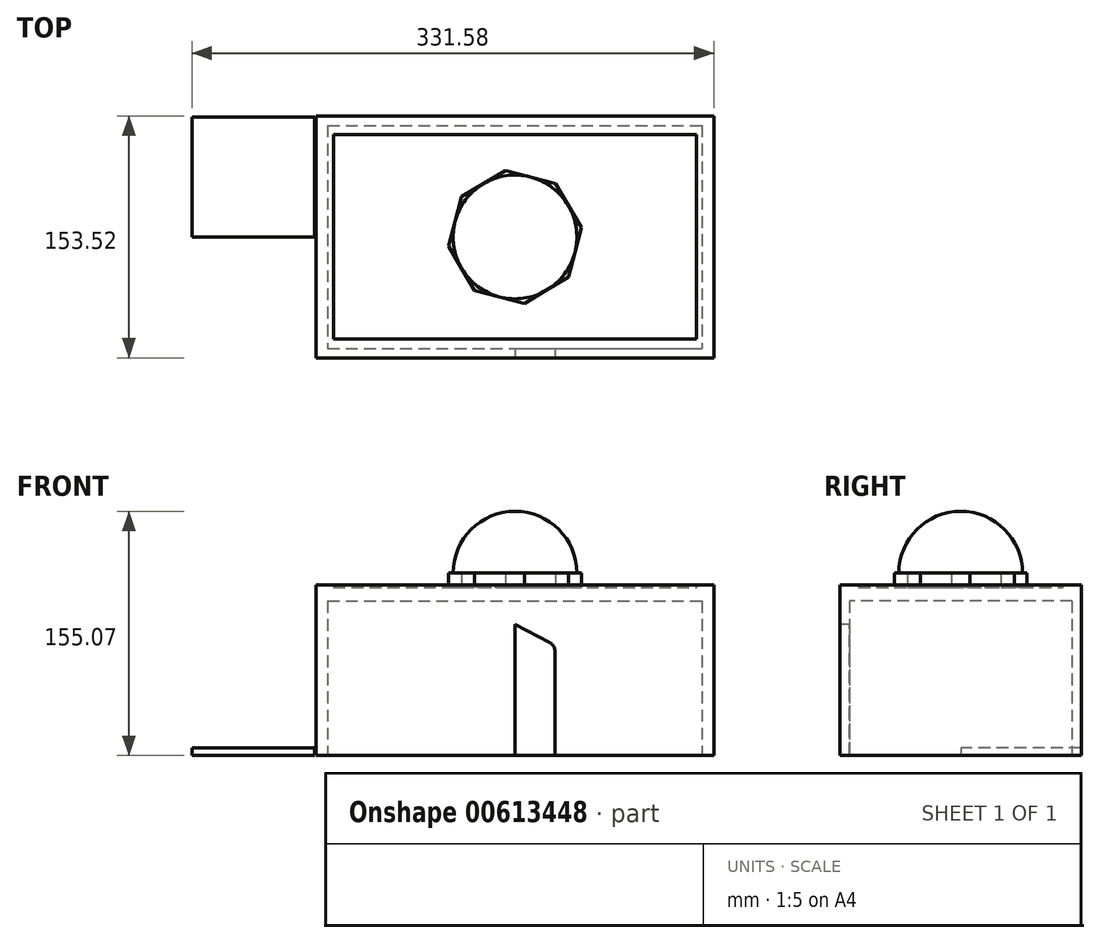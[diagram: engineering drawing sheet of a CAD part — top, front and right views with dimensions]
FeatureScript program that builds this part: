
annotation { "Feature Type Name" : "Feature", "Feature Type Description" : "" }
export const myFeature = defineFeature(function(context is Context, id is Id, definition is map)
    precondition{}
    {
        {
            var Q0;
            Q0=qCreatedBy(makeId("Top.planeOp"),FACE);
            var sketch = newSketch(context, id + "F0", { "sketchPlane" : qUnion([Q0])});
            skLineSegment(sketch, "E0.bottom", {"start": v(126.34, -76.76) * mm, "end": v(-126.34, -76.76) * mm});
            skLineSegment(sketch, "E0.top", {"start": v(126.34, 76.76) * mm, "end": v(-126.34, 76.76) * mm});
            skLineSegment(sketch, "E0.left", {"start": v(126.34, -76.76) * mm, "end": v(126.34, 76.76) * mm});
            skLineSegment(sketch, "E0.right", {"start": v(-126.34, -76.76) * mm, "end": v(-126.34, 76.76) * mm});
            skPoint(sketch, "E0.middle", {"position": v(0, 0) * mm});
            skSolve(sketch);
        }
        {
            var Q0;
            Q0 = qSketchRegion(id + "F0", true);
            extrude(context, id + "F1", {"entities" : qUnion([Q0]), "depth" : 106.63 * mm, "offsetDistance" : 25.4 * mm});
        }
        {
            var Q0;
            Q0=makeQuery(id+"F1.opExtrude","CAP_FACE",FACE,{"disambiguationData":[OSD([sQuery(id+"F0.wireOp",EDGE,"E0.bottom"),sQuery(id+"F0.wireOp",EDGE,"E0.top"),sQuery(id+"F0.wireOp",EDGE,"E0.left"),sQuery(id+"F0.wireOp",EDGE,"E0.right")])],"isStart":false});
            var sketch = newSketch(context, id + "F2", { "sketchPlane" : qUnion([Q0])});
            skCircle(sketch, "E1.cCircle", {"center": v(0, 0) * mm, "radius": 39.31 * mm, "construction": true});
            skLineSegment(sketch, "E1.0", {"start": v(-25.62, -33.98) * mm, "end": v(-42.14, -5.91) * mm});
            skLineSegment(sketch, "E1.1", {"start": v(-42.14, -5.91) * mm, "end": v(-33.98, 25.62) * mm});
            skLineSegment(sketch, "E1.2", {"start": v(-33.98, 25.62) * mm, "end": v(-5.91, 42.14) * mm});
            skLineSegment(sketch, "E1.3", {"start": v(-5.91, 42.14) * mm, "end": v(25.62, 33.98) * mm});
            skLineSegment(sketch, "E1.4", {"start": v(25.62, 33.98) * mm, "end": v(42.14, 5.91) * mm});
            skLineSegment(sketch, "E1.5", {"start": v(42.14, 5.91) * mm, "end": v(33.98, -25.62) * mm});
            skLineSegment(sketch, "E1.6", {"start": v(33.98, -25.62) * mm, "end": v(5.91, -42.14) * mm});
            skLineSegment(sketch, "E1.7", {"start": v(5.91, -42.14) * mm, "end": v(-25.62, -33.98) * mm});
            skPoint(sketch, "E1.0.midPoint", {"position": v(-33.88, -19.94) * mm});
            skSolve(sketch);
        }
        {
            var Q0;
            Q0 = qSketchRegion(id + "F2", true);
            extrude(context, id + "F3", {"entities" : qUnion([Q0]), "operationType" : NewBodyOperationType.ADD, "depth" : 9.12 * mm, "offsetDistance" : 25.4 * mm});
        }
        {
            var Q0;
            Q0=makeQuery(id+"F3.opExtrude","CAP_FACE",FACE,{"disambiguationData":[OSD([sQuery(id+"F2.wireOp",EDGE,"E1.0"),sQuery(id+"F2.wireOp",EDGE,"E1.1"),sQuery(id+"F2.wireOp",EDGE,"E1.2"),sQuery(id+"F2.wireOp",EDGE,"E1.3"),sQuery(id+"F2.wireOp",EDGE,"E1.4"),sQuery(id+"F2.wireOp",EDGE,"E1.5"),sQuery(id+"F2.wireOp",EDGE,"E1.6"),sQuery(id+"F2.wireOp",EDGE,"E1.7")])],"isStart":false});
            var sketch = newSketch(context, id + "F4", { "sketchPlane" : qUnion([Q0])});
            skCircle(sketch, "E2", {"center": v(0, 0) * mm, "radius": 39.31 * mm});
            skLineSegment(sketch, "E3", {"start": v(-42.14, -5.91) * mm, "end": v(42.14, 5.91) * mm});
            skSolve(sketch);
        }
        {
            var Q0;
            {var subQ0=sQuery(id+"F4.wireOp",EDGE,"E2");var subQ5=sQuery(id+"F4.wireOp",EDGE,"E3");var subQ6=makeQuery(id+"F4.imprint","INTERSECT",VERTEX,{"disambiguationData":[OD(0.0)],"derivedFrom":[subQ0,subQ5]});Q0=makeQuery(id+"F4.imprint","IMPRINT",FACE,{"disambiguationData":[TD([[makeQuery(id+"F4.imprint","IMPRINT",EDGE,{"disambiguationData":[TD([[subQ6,-1.0]])],"derivedFrom":subQ0}),1.0]])]});}
            var Q1;
            Q1=sQuery(id+"F4.wireOp",EDGE,"E3");
            revolve(context, id + "F5", {"operationType" : NewBodyOperationType.ADD, "entities" : qUnion([Q0]), "axis" : qUnion([Q1]), "revolveType" : RevolveType.FULL});
        }
        {
            var Q0;
            Q0=makeQuery(id+"F1.opExtrude","CAP_FACE",FACE,{"disambiguationData":[OSD([sQuery(id+"F0.wireOp",EDGE,"E0.bottom"),sQuery(id+"F0.wireOp",EDGE,"E0.top"),sQuery(id+"F0.wireOp",EDGE,"E0.left"),sQuery(id+"F0.wireOp",EDGE,"E0.right")])],"isStart":false});
            var sketch = newSketch(context, id + "F6", { "sketchPlane" : qUnion([Q0])});
            skLineSegment(sketch, "E4.bottom", {"start": v(-115.35, -64.9) * mm, "end": v(115.35, -64.9) * mm});
            skLineSegment(sketch, "E4.top", {"start": v(-115.35, 64.9) * mm, "end": v(115.35, 64.9) * mm});
            skLineSegment(sketch, "E4.left", {"start": v(-115.35, -64.9) * mm, "end": v(-115.35, 64.9) * mm});
            skLineSegment(sketch, "E4.right", {"start": v(115.35, -64.9) * mm, "end": v(115.35, 64.9) * mm});
            skPoint(sketch, "E4.middle", {"position": v(0, 0) * mm});
            skSolve(sketch);
        }
        {
            var Q0;
            Q0=makeQuery(id+"F6.imprint","IMPRINT",FACE,{"disambiguationData":[TD([[makeQuery(id+"F6.imprint","IMPRINT",EDGE,{"derivedFrom":sQuery(id+"F6.wireOp",EDGE,"E4.bottom")}),-1.0]])]});
            var Q1;
            Q1=makeQuery(id+"F6.imprint","IMPRINT",FACE,{"disambiguationData":[TD([[makeQuery(id+"F6.imprint","IMPRINT",EDGE,{"derivedFrom":makeQuery(id+"F3.opExtrude","CAP_EDGE",EDGE,{"disambiguationData":[OSD([sQuery(id+"F2.wireOp",EDGE,"E1.0")])],"isStart":true})}),-1.0]])]});
            extrude(context, id + "F7", {"entities" : qUnion([Q0, Q1]), "operationType" : NewBodyOperationType.ADD, "depth" : 1.62 * mm, "offsetDistance" : 25.4 * mm});
        }
        {
            var Q0;
            {var subQ0=sQuery(id+"F0.wireOp",EDGE,"E0.bottom");Q0=makeQuery(id+"F7.boolean.opBoolean","MERGE",FACE,{"derivedFrom":[makeQuery(id+"F1.opExtrude","SWEPT_FACE",FACE,{"disambiguationData":[OSD([subQ0])]}),makeQuery(id+"F7.opExtrude","SWEPT_FACE",FACE,{"disambiguationData":[OSD([subQ0])]})]});}
            var sketch = newSketch(context, id + "F8", { "sketchPlane" : qUnion([Q0])});
            skLineSegment(sketch, "E5", {"start": v(0, 0) * mm, "end": v(0, 108.25) * mm});
            skLineSegment(sketch, "E6", {"start": v(0, 83.1) * mm, "end": v(21.91, 71.88) * mm});
            skLineSegment(sketch, "E7", {"start": v(25.37, 66.23) * mm, "end": v(25.37, 0) * mm});
            skLineSegment(sketch, "E8", {"start": v(25.37, 0) * mm, "end": v(0, 0) * mm});
            skLineSegment(sketch, "E9", {"start": v(0, 83.1) * mm, "end": v(0, 0) * mm});
            skLineSegment(sketch, "E10.MirrorCS", {"start": v(0, 83.1) * mm, "end": v(-21.91, 71.88) * mm});
            skLineSegment(sketch, "E11.MirrorCS", {"start": v(-25.37, 66.23) * mm, "end": v(-25.37, 0) * mm});
            skLineSegment(sketch, "E12.MirrorCS", {"start": v(-25.37, 0) * mm, "end": v(0, 0) * mm});
            skPoint(sketch, "E13.visualSharp", {"position": v(-25.37, 70.12) * mm});
            skArc(sketch, "E13.filletArc", {"start": v(-21.91, 71.88) * mm, "mid": v(-24.44, 69.54) * mm, "end": v(-25.37, 66.23) * mm});
            skPoint(sketch, "E14.visualSharp", {"position": v(25.37, 70.12) * mm});
            skArc(sketch, "E14.filletArc", {"start": v(25.37, 66.23) * mm, "mid": v(24.44, 69.54) * mm, "end": v(21.91, 71.88) * mm});
            skSolve(sketch);
        }
        {
            var Q0;
            Q0=makeQuery(id+"F8.imprint","IMPRINT",FACE,{"disambiguationData":[TD([[makeQuery(id+"F8.imprint","IMPRINT",EDGE,{"derivedFrom":sQuery(id+"F8.wireOp",EDGE,"E6")}),-1.0]])]});
            var Q1;
            Q1=makeQuery(id+"F8.imprint","IMPRINT",FACE,{"disambiguationData":[TD([[makeQuery(id+"F8.imprint","IMPRINT",EDGE,{"derivedFrom":sQuery(id+"F8.wireOp",EDGE,"E9")}),-1.0]])]});
            extrude(context, id + "F9", {"entities" : qUnion([Q0, Q1]), "operationType" : NewBodyOperationType.REMOVE, "oppositeDirection" : true, "depth" : 6.33 * mm, "offsetDistance" : 25.4 * mm});
        }
        {
            var Q0;
            Q0=makeQuery(id+"F1.opExtrude","CAP_FACE",FACE,{"disambiguationData":[OSD([sQuery(id+"F0.wireOp",EDGE,"E0.bottom"),sQuery(id+"F0.wireOp",EDGE,"E0.top"),sQuery(id+"F0.wireOp",EDGE,"E0.left"),sQuery(id+"F0.wireOp",EDGE,"E0.right")])],"isStart":true});
            var sketch = newSketch(context, id + "F10", { "sketchPlane" : qUnion([Q0])});
            skLineSegment(sketch, "E15.bottom", {"start": v(-118.89, -70.76) * mm, "end": v(118.89, -70.76) * mm});
            skLineSegment(sketch, "E15.top", {"start": v(-118.89, 70.76) * mm, "end": v(118.89, 70.76) * mm});
            skLineSegment(sketch, "E15.left", {"start": v(-118.89, -70.76) * mm, "end": v(-118.89, 70.76) * mm});
            skLineSegment(sketch, "E15.right", {"start": v(118.89, -70.76) * mm, "end": v(118.89, 70.76) * mm});
            skPoint(sketch, "E15.middle", {"position": v(0, 0) * mm});
            skSolve(sketch);
        }
        {
            var Q0;
            Q0 = qSketchRegion(id + "F10", true);
            extrude(context, id + "F11", {"entities" : qUnion([Q0]), "operationType" : NewBodyOperationType.REMOVE, "oppositeDirection" : true, "depth" : 98.04 * mm, "offsetDistance" : 25.4 * mm});
        }
        {
            var Q0;
            Q0=qCreatedBy(makeId("Top.planeOp"),FACE);
            var sketch = newSketch(context, id + "F12", { "sketchPlane" : qUnion([Q0])});
            skLineSegment(sketch, "E16.bottom", {"start": v(-127.43, 76.23) * mm, "end": v(-205.24, 76.23) * mm});
            skLineSegment(sketch, "E16.top", {"start": v(-127.43, 0) * mm, "end": v(-205.24, 0) * mm});
            skLineSegment(sketch, "E16.left", {"start": v(-127.43, 76.23) * mm, "end": v(-127.43, 0) * mm});
            skLineSegment(sketch, "E16.right", {"start": v(-205.24, 76.23) * mm, "end": v(-205.24, 0) * mm});
            skSolve(sketch);
        }
        {
            var Q0;
            Q0 = qSketchRegion(id + "F12", true);
            extrude(context, id + "F13", {"entities" : qUnion([Q0]), "depth" : 4.64 * mm, "offsetDistance" : 25.4 * mm});
        }
    });
